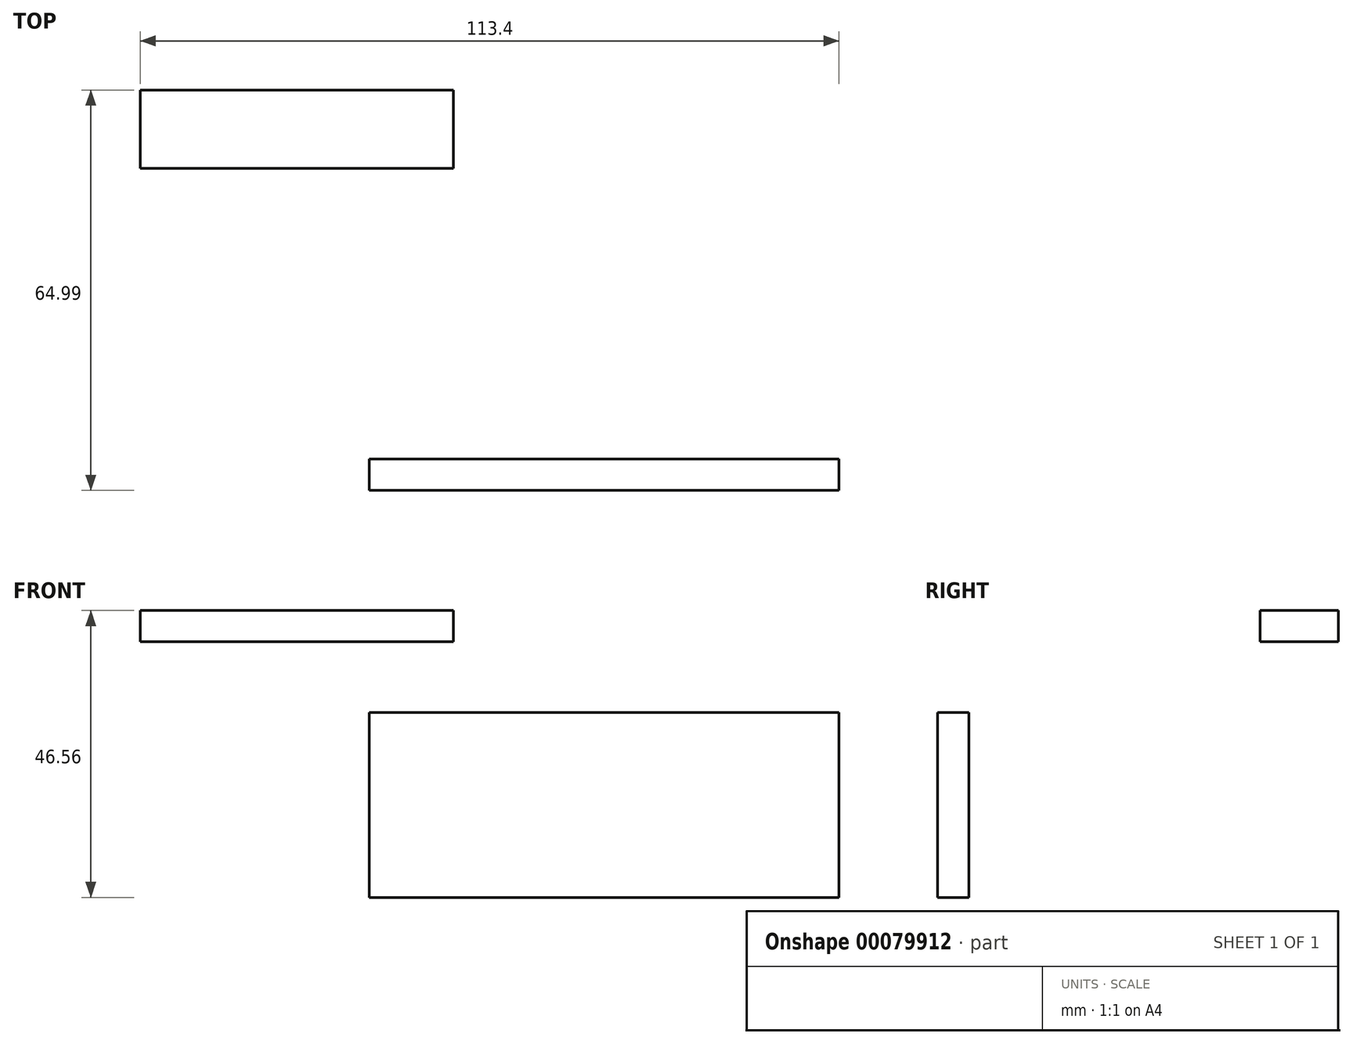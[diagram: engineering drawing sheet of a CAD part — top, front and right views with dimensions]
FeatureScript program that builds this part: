
annotation { "Feature Type Name" : "Feature", "Feature Type Description" : "" }
export const myFeature = defineFeature(function(context is Context, id is Id, definition is map)
    precondition{}
    {
        {
            var Q0;
            Q0=qCreatedBy(makeId("Front.planeOp"),FACE);
            var sketch = newSketch(context, id + "F0", { "sketchPlane" : qUnion([Q0])});
            skLineSegment(sketch, "E0.bottom", {"start": v(-37.46, -11.48) * mm, "end": v(38.74, -11.48) * mm});
            skLineSegment(sketch, "E0.top", {"start": v(-37.46, -41.48) * mm, "end": v(38.74, -41.48) * mm});
            skLineSegment(sketch, "E0.left", {"start": v(-37.46, -11.48) * mm, "end": v(-37.46, -41.48) * mm});
            skLineSegment(sketch, "E0.right", {"start": v(38.74, -11.48) * mm, "end": v(38.74, -41.48) * mm});
            skSolve(sketch);
        }
        {
            var Q0;
            Q0=makeQuery(id+"F0.imprint","IMPRINT",FACE,{"disambiguationData":[TD([[makeQuery(id+"F0.imprint","IMPRINT",EDGE,{"derivedFrom":sQuery(id+"F0.wireOp",EDGE,"E0.bottom")}),-1.0]])]});
            extrude(context, id + "F1", {"entities" : qUnion([Q0]), "depth" : 5.08 * mm});
        }
        {
            var Q0;
            Q0=qCreatedBy(makeId("Top.planeOp"),FACE);
            var sketch = newSketch(context, id + "F2", { "sketchPlane" : qUnion([Q0])});
            skLineSegment(sketch, "E1.bottom", {"start": v(-74.66, 59.91) * mm, "end": v(-23.86, 59.91) * mm});
            skLineSegment(sketch, "E1.top", {"start": v(-74.66, 47.21) * mm, "end": v(-23.86, 47.21) * mm});
            skLineSegment(sketch, "E1.left", {"start": v(-74.66, 59.91) * mm, "end": v(-74.66, 47.21) * mm});
            skLineSegment(sketch, "E1.right", {"start": v(-23.86, 59.91) * mm, "end": v(-23.86, 47.21) * mm});
            skSolve(sketch);
        }
        {
            var Q0;
            Q0=makeQuery(id+"F2.imprint","IMPRINT",FACE,{"disambiguationData":[TD([[makeQuery(id+"F2.imprint","IMPRINT",EDGE,{"derivedFrom":sQuery(id+"F2.wireOp",EDGE,"E1.bottom")}),-1.0]])]});
            extrude(context, id + "F3", {"entities" : qUnion([Q0]), "depth" : 5.08 * mm});
        }
    });
